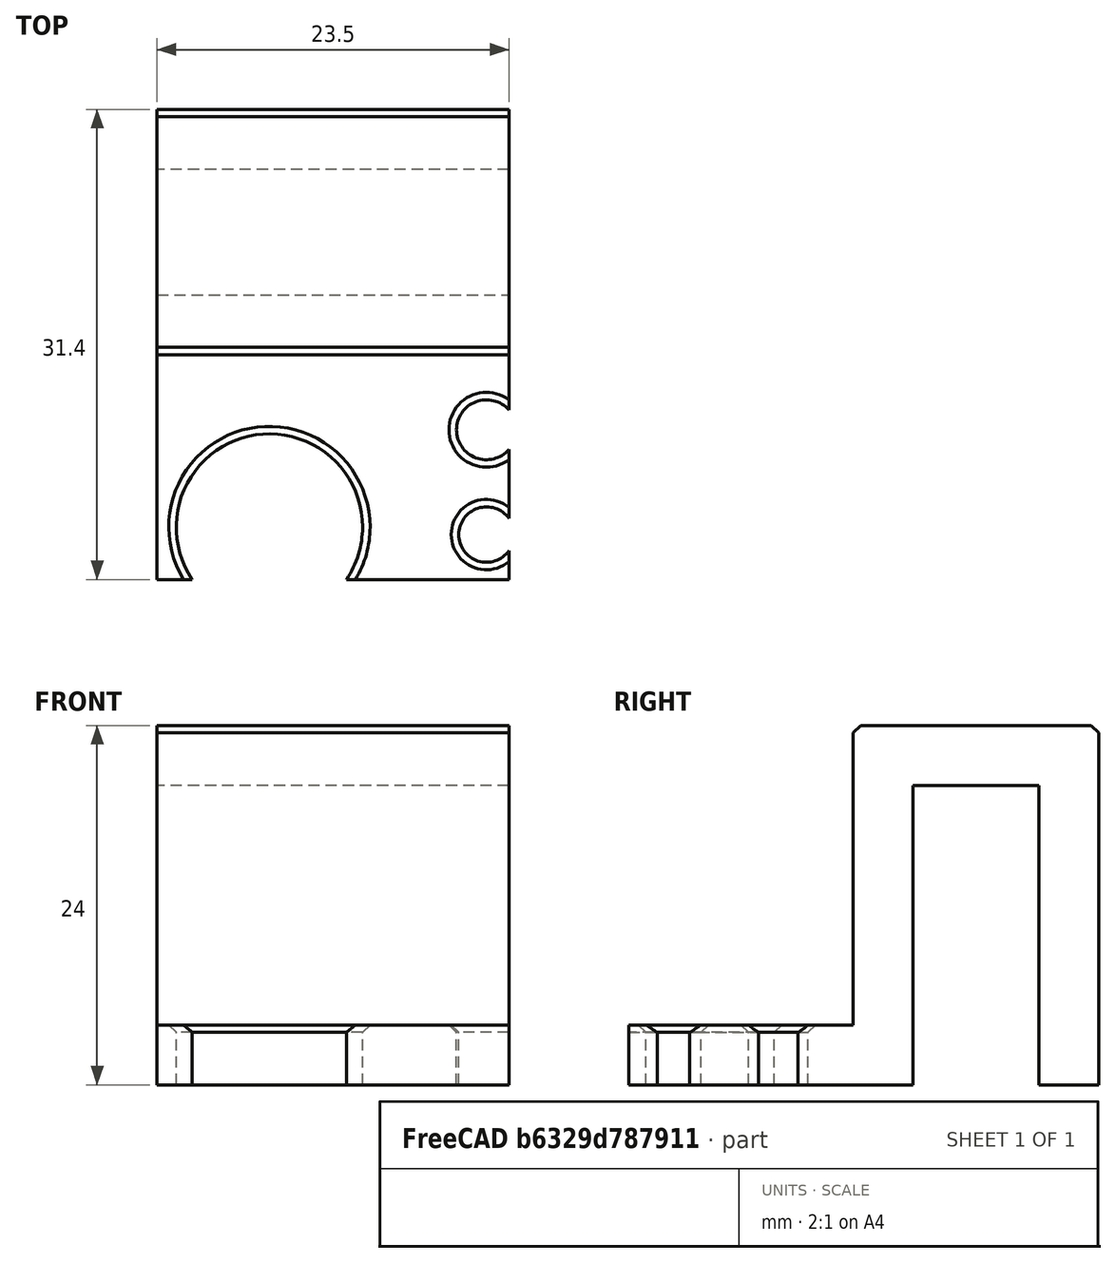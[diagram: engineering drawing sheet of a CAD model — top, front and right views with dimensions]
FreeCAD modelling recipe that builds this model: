
FCSTD DOCUMENT  (FreeCAD 0.18R4 (GitTag))
Label: AquariumHolder_TDS_PH_TEMP
License: All rights reserved
LicenseURL: http://en.wikipedia.org/wiki/All_rights_reserved
objects: Part::Box×5, Part::Cut×4, Part::Cylinder×3, Part::Chamfer×2, Part::MultiFuse×1
note: 15 computed .brp shape members not serialized (recipe doc carries the construction recipe); baked Part::Feature solids carry a one-line shape summary decoded from their .brp

FEATURE [Part::Box] Box  label="Glass"
  AttacherType = Attacher::AttachEngine3D
  Height = 20
  Length = 31
  Placement = pos=(-10,0,0) rot=(0,0,1;0rad)
  Width = 8.4
FEATURE [Part::Cylinder] Cylinder  label="pH_tube"
  Angle = 360
  AttacherType = Attacher::AttachEngine3D
  Height = 10
  Placement = pos=(-2.5,-15.5,0) rot=(0,0,1;0rad)
  Radius = 6.225
FEATURE [Part::Cylinder] Cylinder001  label="Temp_tube"
  Angle = 360
  AttacherType = Attacher::AttachEngine3D
  Height = 10
  Placement = pos=(12,-9,0) rot=(0,0,1;0rad)
  Radius = 2
FEATURE [Part::Cylinder] Cylinder002  label="TDS_tube"
  Angle = 360
  AttacherType = Attacher::AttachEngine3D
  Height = 10
  Placement = pos=(12,-16,0) rot=(0,0,1;0rad)
  Radius = 1.85
FEATURE [Part::Box] Box001  label="Front"
  AttacherType = Attacher::AttachEngine3D
  Height = 24
  Length = 23.5
  Placement = pos=(-10,-4,0) rot=(0,0,1;0rad)
  Width = 4
FEATURE [Part::Box] Box002  label="Bottom"
  AttacherType = Attacher::AttachEngine3D
  Height = 4
  Length = 23.5
  Placement = pos=(-10,-19,0) rot=(0,0,1;0rad)
  Width = 16
FEATURE [Part::Box] Box003  label="Back"
  AttacherType = Attacher::AttachEngine3D
  Height = 24
  Length = 23.5
  Placement = pos=(-10,8.4,0) rot=(0,0,1;0rad)
  Width = 4
FEATURE [Part::Box] Box004  label="Top"
  AttacherType = Attacher::AttachEngine3D
  Height = 4
  Length = 23.5
  Placement = pos=(-10,-4,20) rot=(0,0,1;0rad)
  Width = 14
FEATURE [Part::MultiFuse] Fusion
  Shapes = -> [Box004,Box003,Box002,Box001]
FEATURE [Part::Cut] Cut
  Base = -> Fusion
  Tool = -> Cylinder002
FEATURE [Part::Cut] Cut001
  Base = -> Cut
  Tool = -> Cylinder001
FEATURE [Part::Cut] Cut002
  Base = -> Cut001
  Tool = -> Cylinder
FEATURE [Part::Cut] Cut003
  Base = -> Cut002
  Tool = -> Box
FEATURE [Part::Chamfer] Chamfer
  Base = -> Cut003
  Edges = 4 edges r=0.5: [Edge40,Edge42,Edge45,Edge46]
FEATURE [Part::Chamfer] Chamfer001
  Base = -> Chamfer
  Edges = 2 edges r=0.5: [Edge54,Edge96]
